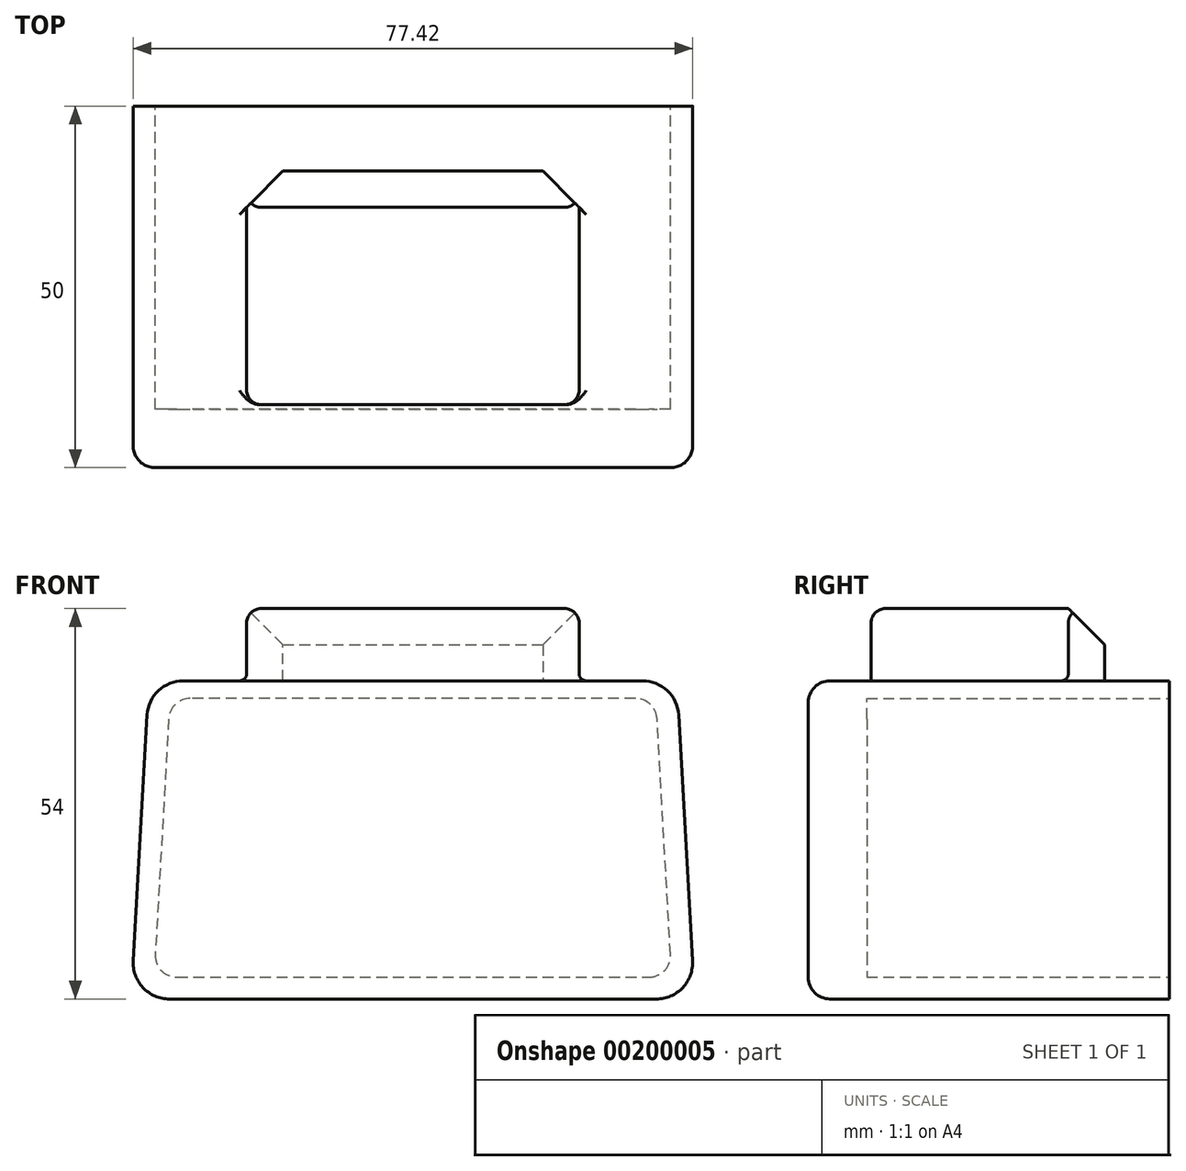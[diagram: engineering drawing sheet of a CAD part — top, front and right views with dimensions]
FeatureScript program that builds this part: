
annotation { "Feature Type Name" : "Feature", "Feature Type Description" : "" }
export const myFeature = defineFeature(function(context is Context, id is Id, definition is map)
    precondition{}
    {
        {
            var Q0;
            Q0=qCreatedBy(makeId("Front.planeOp"),FACE);
            var sketch = newSketch(context, id + "F0", { "sketchPlane" : qUnion([Q0])});
            skLineSegment(sketch, "E0.bottom", {"start": v(0, 0) * mm, "end": v(1000, 0) * mm, "construction": true});
            skLineSegment(sketch, "E0.top", {"start": v(0, 1000) * mm, "end": v(1000, 1000) * mm, "construction": true});
            skLineSegment(sketch, "E0.left", {"start": v(0, 0) * mm, "end": v(0, 1000) * mm, "construction": true});
            skLineSegment(sketch, "E0.right", {"start": v(1000, 0) * mm, "end": v(1000, 1000) * mm, "construction": true});
            skLineSegment(sketch, "E1.bottom", {"start": v(0, 0) * mm, "end": v(100, 0) * mm, "construction": true});
            skLineSegment(sketch, "E1.top", {"start": v(0, 100) * mm, "end": v(100, 100) * mm, "construction": true});
            skLineSegment(sketch, "E1.left", {"start": v(0, 0) * mm, "end": v(0, 100) * mm, "construction": true});
            skLineSegment(sketch, "E1.right", {"start": v(100, 0) * mm, "end": v(100, 100) * mm, "construction": true});
            skLineSegment(sketch, "E2.bottom", {"start": v(100, 100) * mm, "end": v(178, 100) * mm, "construction": true});
            skLineSegment(sketch, "E2.top", {"start": v(100, 144) * mm, "end": v(178, 144) * mm, "construction": true});
            skLineSegment(sketch, "E2.left", {"start": v(100, 100) * mm, "end": v(100, 144) * mm, "construction": true});
            skLineSegment(sketch, "E2.right", {"start": v(178, 100) * mm, "end": v(178, 144) * mm, "construction": true});
            skLineSegment(sketch, "E3.bottom", {"start": v(116, 144) * mm, "end": v(162, 144) * mm, "construction": true});
            skLineSegment(sketch, "E3.top", {"start": v(116, 154) * mm, "end": v(162, 154) * mm, "construction": true});
            skLineSegment(sketch, "E3.left", {"start": v(116, 144) * mm, "end": v(116, 154) * mm, "construction": true});
            skLineSegment(sketch, "E3.right", {"start": v(162, 144) * mm, "end": v(162, 154) * mm, "construction": true});
            skPoint(sketch, "E4", {"position": v(139, 144) * mm});
            skLineSegment(sketch, "E5", {"start": v(100, 100) * mm, "end": v(102.5, 144) * mm, "construction": true});
            skLineSegment(sketch, "E6", {"start": v(178, 100) * mm, "end": v(175.5, 144) * mm, "construction": true});
            skLineSegment(sketch, "E7", {"start": v(102.5, 182.81) * mm, "end": v(175.5, 182.81) * mm, "construction": true});
            skPoint(sketch, "E8", {"position": v(139, 182.81) * mm});
            skSolve(sketch);
        }
        {
            var Q0;
            Q0=qCreatedBy(makeId("Front.planeOp"),FACE);
            var sketch = newSketch(context, id + "F1", { "sketchPlane" : qUnion([Q0])});
            skLineSegment(sketch, "E9", {"start": v(105.3, 100) * mm, "end": v(172.7, 100) * mm});
            skLineSegment(sketch, "E10", {"start": v(175.77, 139.28) * mm, "end": v(177.7, 105.28) * mm});
            skLineSegment(sketch, "E11", {"start": v(102.23, 139.28) * mm, "end": v(100.3, 105.28) * mm});
            skLineSegment(sketch, "E12", {"start": v(107.22, 144) * mm, "end": v(115, 144) * mm});
            skLineSegment(sketch, "E13", {"start": v(116, 145) * mm, "end": v(116, 152) * mm});
            skLineSegment(sketch, "E14", {"start": v(118, 154) * mm, "end": v(160, 154) * mm});
            skLineSegment(sketch, "E15", {"start": v(162, 152) * mm, "end": v(162, 145) * mm});
            skLineSegment(sketch, "E16", {"start": v(163, 144) * mm, "end": v(170.78, 144) * mm});
            skPoint(sketch, "E17.visualSharp", {"position": v(116, 154) * mm});
            skArc(sketch, "E17.filletArc", {"start": v(118, 154) * mm, "mid": v(116.59, 153.41) * mm, "end": v(116, 152) * mm});
            skPoint(sketch, "E18.visualSharp", {"position": v(162, 154) * mm});
            skArc(sketch, "E18.filletArc", {"start": v(162, 152) * mm, "mid": v(161.41, 153.41) * mm, "end": v(160, 154) * mm});
            skPoint(sketch, "E19.visualSharp", {"position": v(102.5, 144) * mm});
            skArc(sketch, "E19.filletArc", {"start": v(107.22, 144) * mm, "mid": v(103.8, 142.63) * mm, "end": v(102.23, 139.28) * mm});
            skPoint(sketch, "E20.visualSharp", {"position": v(175.5, 144) * mm});
            skArc(sketch, "E20.filletArc", {"start": v(175.77, 139.28) * mm, "mid": v(174.2, 142.63) * mm, "end": v(170.78, 144) * mm});
            skPoint(sketch, "E21.visualSharp", {"position": v(178, 100) * mm});
            skArc(sketch, "E21.filletArc", {"start": v(172.7, 100) * mm, "mid": v(176.34, 101.57) * mm, "end": v(177.7, 105.28) * mm});
            skPoint(sketch, "E22.visualSharp", {"position": v(100, 100) * mm});
            skArc(sketch, "E22.filletArc", {"start": v(100.3, 105.28) * mm, "mid": v(101.66, 101.57) * mm, "end": v(105.3, 100) * mm});
            skPoint(sketch, "E23.visualSharp", {"position": v(116, 144) * mm});
            skArc(sketch, "E23.filletArc", {"start": v(115, 144) * mm, "mid": v(115.7, 144.3) * mm, "end": v(116, 145) * mm});
            skPoint(sketch, "E24.visualSharp", {"position": v(162, 144) * mm});
            skArc(sketch, "E24.filletArc", {"start": v(162, 145) * mm, "mid": v(162.3, 144.3) * mm, "end": v(163, 144) * mm});
            skLineSegment(sketch, "E25", {"start": v(107.22, 144) * mm, "end": v(170.78, 144) * mm});
            skSolve(sketch);
        }
        {
            var Q0;
            Q0=makeQuery(id+"F1.imprint","IMPRINT",FACE,{"disambiguationData":[TD([[makeQuery(id+"F1.imprint","IMPRINT",EDGE,{"derivedFrom":sQuery(id+"F1.wireOp",EDGE,"E9")}),1.0]])]});
            extrude(context, id + "F2", {"entities" : qUnion([Q0]), "oppositeDirection" : true, "depth" : 50 * mm});
        }
        {
            var Q0;
            Q0=makeQuery(id+"F1.imprint","IMPRINT",FACE,{"disambiguationData":[TD([[makeQuery(id+"F1.imprint","IMPRINT",EDGE,{"derivedFrom":sQuery(id+"F1.wireOp",EDGE,"E13")}),-1.0]])]});
            extrude(context, id + "F3", {"entities" : qUnion([Q0]), "operationType" : NewBodyOperationType.ADD, "oppositeDirection" : true, "depth" : 41 * mm, "hasSecondDirection" : true, "secondDirectionOppositeDirection" : true, "secondDirectionDepth" : 8.7 * mm});
        }
        {
            var Q0;
            Q0=makeQuery(id+"F3.opExtrude","CAP_EDGE",EDGE,{"disambiguationData":[OSD([sQuery(id+"F1.wireOp",EDGE,"E14")])],"isStart":true});
            fillet(context, id + "F4", {"entities" : qUnion([Q0]), "radius" : 2 * mm, "tangentPropagation" : true, "allowEdgeOverflow" : false});
        }
        {
            var Q0;
            Q0=makeQuery(id+"F3.opExtrude","CAP_EDGE",EDGE,{"disambiguationData":[OSD([sQuery(id+"F1.wireOp",EDGE,"E14")])],"isStart":false});
            var Q1;
            Q1=makeQuery(id+"F3.opExtrude","CAP_EDGE",EDGE,{"disambiguationData":[OSD([sQuery(id+"F1.wireOp",EDGE,"E13")])],"isStart":false});
            var Q2;
            Q2=makeQuery(id+"F3.opExtrude","CAP_EDGE",EDGE,{"disambiguationData":[OSD([sQuery(id+"F1.wireOp",EDGE,"E15")])],"isStart":false});
            chamfer(context, id + "F5", {"entities" : qUnion([Q0, Q1, Q2]), "chamferType" : ChamferType.TWO_OFFSETS, "width1" : 5 * mm, "oppositeDirection" : true, "width2" : 5 * mm});
        }
        {
            var Q0;
            Q0=makeQuery(id+"F2.opExtrude","CAP_EDGE",EDGE,{"disambiguationData":[OSD([sQuery(id+"F1.wireOp",EDGE,"E25")])],"isStart":true});
            fillet(context, id + "F6", {"entities" : qUnion([Q0]), "radius" : 3 * mm, "tangentPropagation" : true, "allowEdgeOverflow" : false});
        }
        {
            var Q0;
            Q0=makeQuery(id+"F2.opExtrude","CAP_FACE",FACE,{"disambiguationData":[OSD([sQuery(id+"F1.wireOp",EDGE,"E9"),sQuery(id+"F1.wireOp",EDGE,"E10"),sQuery(id+"F1.wireOp",EDGE,"E11"),sQuery(id+"F1.wireOp",EDGE,"E19.filletArc"),sQuery(id+"F1.wireOp",EDGE,"E20.filletArc"),sQuery(id+"F1.wireOp",EDGE,"E21.filletArc"),sQuery(id+"F1.wireOp",EDGE,"E22.filletArc"),sQuery(id+"F1.wireOp",EDGE,"E25")])],"isStart":false});
            var sketch = newSketch(context, id + "F7", { "sketchPlane" : qUnion([Q0])});
            skLineSegment(sketch, "E26", {"start": v(-169.8, 141.57) * mm, "end": v(-108.2, 141.57) * mm});
            skLineSegment(sketch, "E27", {"start": v(-105.2, 138.74) * mm, "end": v(-103.36, 106.17) * mm});
            skLineSegment(sketch, "E28", {"start": v(-106.35, 103) * mm, "end": v(-171.65, 103) * mm});
            skLineSegment(sketch, "E29", {"start": v(-174.64, 106.17) * mm, "end": v(-172.8, 138.74) * mm});
            skPoint(sketch, "E30", {"position": v(-139, 141.57) * mm});
            skPoint(sketch, "E31", {"position": v(-173.73, 122.28) * mm});
            skPoint(sketch, "E32", {"position": v(-176.73, 122.28) * mm});
            skPoint(sketch, "E33.visualSharp", {"position": v(-172.63, 141.57) * mm});
            skArc(sketch, "E33.filletArc", {"start": v(-169.8, 141.57) * mm, "mid": v(-171.86, 140.75) * mm, "end": v(-172.8, 138.74) * mm});
            skPoint(sketch, "E34.visualSharp", {"position": v(-105.37, 141.57) * mm});
            skArc(sketch, "E34.filletArc", {"start": v(-105.2, 138.74) * mm, "mid": v(-106.14, 140.75) * mm, "end": v(-108.2, 141.57) * mm});
            skPoint(sketch, "E35.visualSharp", {"position": v(-103.18, 103) * mm});
            skArc(sketch, "E35.filletArc", {"start": v(-106.35, 103) * mm, "mid": v(-104.17, 103.94) * mm, "end": v(-103.36, 106.17) * mm});
            skPoint(sketch, "E36.visualSharp", {"position": v(-174.82, 103) * mm});
            skArc(sketch, "E36.filletArc", {"start": v(-174.64, 106.17) * mm, "mid": v(-173.83, 103.94) * mm, "end": v(-171.65, 103) * mm});
            skSolve(sketch);
        }
        {
            var Q0;
            Q0=makeQuery(id+"F7.imprint","IMPRINT",FACE,{"disambiguationData":[TD([[makeQuery(id+"F7.imprint","IMPRINT",EDGE,{"derivedFrom":sQuery(id+"F7.wireOp",EDGE,"E26")}),-1.0]])]});
            extrude(context, id + "F8", {"entities" : qUnion([Q0]), "operationType" : NewBodyOperationType.REMOVE, "oppositeDirection" : true, "depth" : 41.9 * mm});
        }
    });
